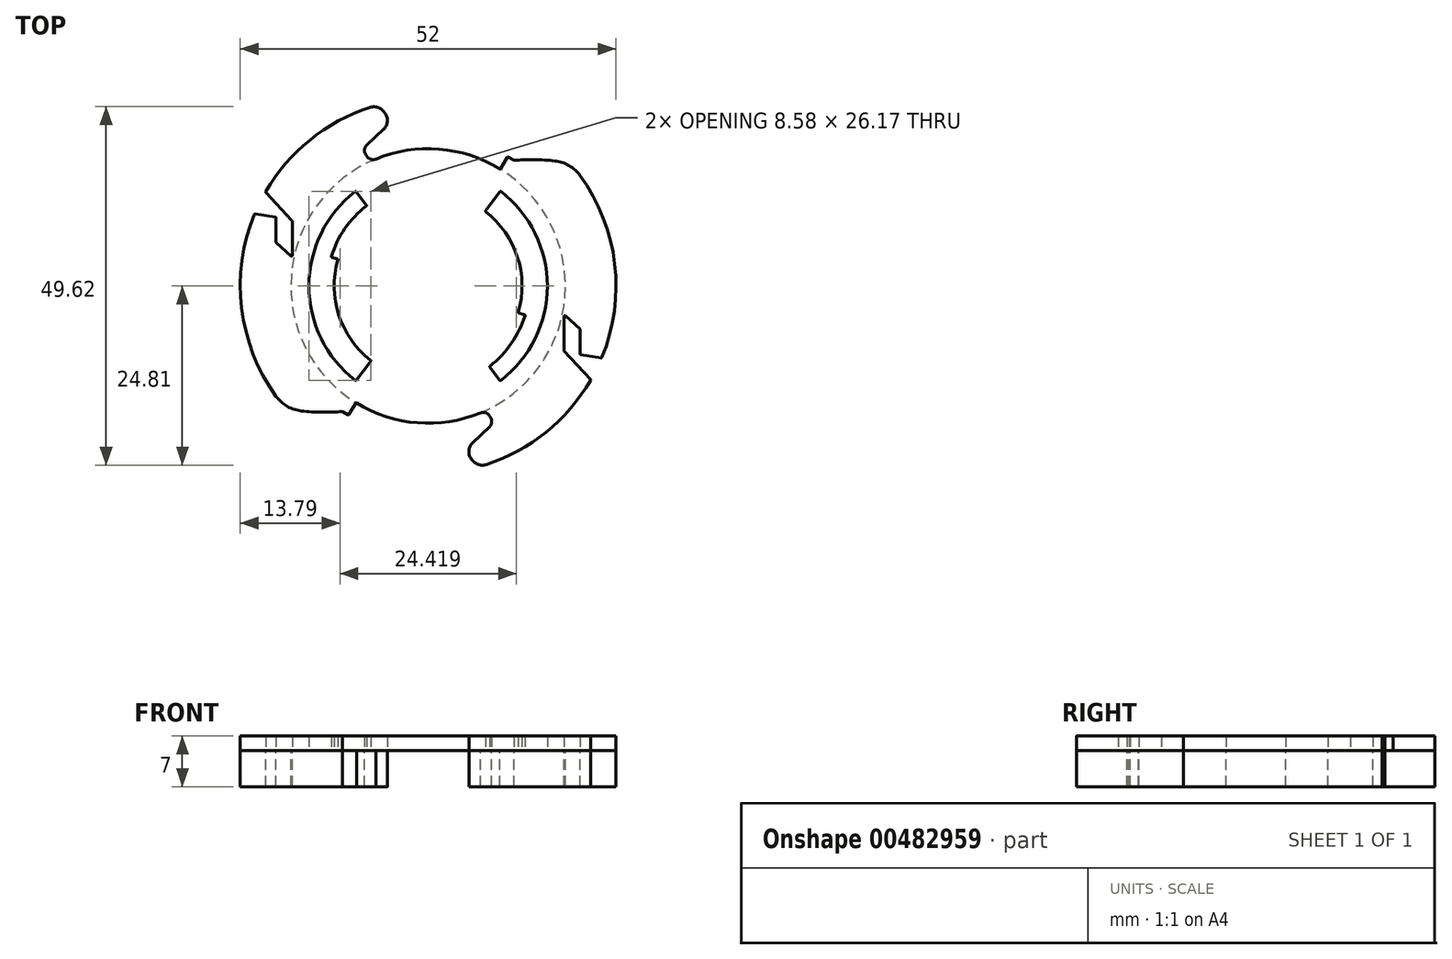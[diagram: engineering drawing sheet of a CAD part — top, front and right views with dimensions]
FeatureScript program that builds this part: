
annotation { "Feature Type Name" : "Feature", "Feature Type Description" : "" }
export const myFeature = defineFeature(function(context is Context, id is Id, definition is map)
    precondition{}
    {
        {
            var Q0;
            Q0=qCreatedBy(makeId("Top.planeOp"),FACE);
            var sketch = newSketch(context, id + "F0", { "sketchPlane" : qUnion([Q0])});
            skArc(sketch, "E0", {"start": v(-9.91, -16.2) * mm, "mid": v(-1.5, -18.94) * mm, "end": v(7.25, -17.56) * mm});
            skArc(sketch, "E1", {"start": v(-10.08, 13.06) * mm, "mid": v(-16.5, 0) * mm, "end": v(-10.08, -13.06) * mm});
            skArc(sketch, "E2", {"start": v(-8.56, 11.08) * mm, "mid": v(-11.52, 7.96) * mm, "end": v(-13.39, 4.1) * mm});
            skArc(sketch, "E3", {"start": v(-12.49, 3.62) * mm, "mid": v(-12.36, -4.03) * mm, "end": v(-7.96, -10.28) * mm});
            skLineSegment(sketch, "E4", {"start": v(-26, 0) * mm, "end": v(26, 0) * mm, "construction": true});
            skLineSegment(sketch, "E5", {"start": v(0, 26) * mm, "end": v(0, -26) * mm, "construction": true});
            skLineSegment(sketch, "E6", {"start": v(9.94, 13.04) * mm, "end": v(7.94, 10.42) * mm});
            skLineSegment(sketch, "E7.MirrorCS", {"start": v(-9.94, 13.04) * mm, "end": v(-8.55, 11.22) * mm});
            skArc(sketch, "E8.trimOffspring", {"start": v(12.49, -3.62) * mm, "mid": v(12.36, 4.03) * mm, "end": v(7.96, 10.28) * mm});
            skArc(sketch, "E9.trimOffspring", {"start": v(8.56, -11.08) * mm, "mid": v(11.52, -7.96) * mm, "end": v(13.39, -4.1) * mm});
            skArc(sketch, "E10.trimOffspring", {"start": v(10.08, -13.06) * mm, "mid": v(16.5, 0) * mm, "end": v(10.08, 13.06) * mm});
            skLineSegment(sketch, "E11", {"start": v(13.32, -3.97) * mm, "end": v(12.55, -3.74) * mm});
            skLineSegment(sketch, "E12.trimOffspring", {"start": v(-7.94, -10.42) * mm, "end": v(-9.94, -13.04) * mm});
            skLineSegment(sketch, "E13.trimOffspring", {"start": v(8.55, -11.22) * mm, "end": v(9.94, -13.04) * mm});
            skLineSegment(sketch, "E14.trimOffspring", {"start": v(-12.55, 3.74) * mm, "end": v(-13.32, 3.97) * mm});
            skPoint(sketch, "E15.visualSharp", {"position": v(-7.94, -19.43) * mm});
            skPoint(sketch, "E16.visualSharp", {"position": v(-3.13, -21.98) * mm});
            skPoint(sketch, "E17.visualSharp", {"position": v(-5, -25.51) * mm});
            skPoint(sketch, "E18.visualSharp", {"position": v(7.94, 19.43) * mm});
            skPoint(sketch, "E19.visualSharp", {"position": v(3.13, 21.98) * mm});
            skPoint(sketch, "E20.visualSharp", {"position": v(5, 25.51) * mm});
            skPoint(sketch, "E21.visualSharp", {"position": v(-8.52, 18.97) * mm});
            skPoint(sketch, "E22.visualSharp", {"position": v(-18.02, 18.75) * mm});
            skPoint(sketch, "E23.visualSharp", {"position": v(18.02, -18.75) * mm});
            skPoint(sketch, "E24.start.orphan", {"position": v(7, 17.66) * mm});
            skPoint(sketch, "E25.start.orphan", {"position": v(7, -17.66) * mm});
            skArc(sketch, "E26", {"start": v(8.04, -24.73) * mm, "mid": v(16.33, -20.23) * mm, "end": v(22.48, -13.06) * mm});
            skLineSegment(sketch, "E27", {"start": v(8.46, -17.93) * mm, "end": v(8.64, -18.2) * mm});
            skLineSegment(sketch, "E28", {"start": v(8.5, -19.48) * mm, "end": v(6.17, -21.7) * mm});
            skLineSegment(sketch, "E29", {"start": v(6.1, -24.1) * mm, "end": v(6.28, -24.28) * mm});
            skLineSegment(sketch, "E30", {"start": v(10.05, 16.24) * mm, "end": v(10.95, 17.8) * mm});
            skLineSegment(sketch, "E31", {"start": v(11.09, 17.84) * mm, "end": v(11.87, 17.39) * mm});
            skArc(sketch, "E32", {"start": v(11.87, 17.39) * mm, "mid": v(14.7, 17.48) * mm, "end": v(17.53, 17.31) * mm});
            skPoint(sketch, "E33.start.orphan", {"position": v(-7, 17.66) * mm});
            skPoint(sketch, "E34.end.orphan", {"position": v(-9.17, 18.2) * mm});
            skPoint(sketch, "E35.start.orphan", {"position": v(-7, -17.66) * mm});
            skArc(sketch, "E36", {"start": v(-8.04, 24.73) * mm, "mid": v(-16.33, 20.23) * mm, "end": v(-22.48, 13.06) * mm});
            skLineSegment(sketch, "E37", {"start": v(-8.46, 17.93) * mm, "end": v(-8.64, 18.2) * mm});
            skLineSegment(sketch, "E38", {"start": v(-8.5, 19.48) * mm, "end": v(-6.17, 21.7) * mm});
            skLineSegment(sketch, "E39", {"start": v(-6.1, 24.1) * mm, "end": v(-6.28, 24.28) * mm});
            skLineSegment(sketch, "E40", {"start": v(-10.05, -16.24) * mm, "end": v(-10.95, -17.8) * mm});
            skLineSegment(sketch, "E41", {"start": v(-11.09, -17.84) * mm, "end": v(-11.87, -17.39) * mm});
            skArc(sketch, "E42", {"start": v(-11.87, -17.39) * mm, "mid": v(-14.7, -17.48) * mm, "end": v(-17.53, -17.31) * mm});
            skArc(sketch, "E43.trimOffspring", {"start": v(9.91, 16.2) * mm, "mid": v(1.5, 18.94) * mm, "end": v(-7.25, 17.56) * mm});
            skCircle(sketch, "E44", {"center": v(0, 0) * mm, "radius": 19 * mm, "construction": true});
            skLineSegment(sketch, "E45", {"start": v(23.92, -9.99) * mm, "end": v(21.13, -9.51) * mm});
            skLineSegment(sketch, "E46", {"start": v(21.04, -9.42) * mm, "end": v(21.04, -6.04) * mm});
            skLineSegment(sketch, "E47", {"start": v(21, -5.97) * mm, "end": v(18.97, -4.15) * mm});
            skLineSegment(sketch, "E48", {"start": v(18.8, -4.22) * mm, "end": v(18.8, -8.96) * mm});
            skLineSegment(sketch, "E49", {"start": v(18.83, -9.03) * mm, "end": v(22.47, -12.95) * mm});
            skArc(sketch, "E50.trimOffspring", {"start": v(24.03, -9.93) * mm, "mid": v(25.82, 3.07) * mm, "end": v(21.04, 15.28) * mm});
            skLineSegment(sketch, "E51", {"start": v(-23.92, 9.99) * mm, "end": v(-21.13, 9.51) * mm});
            skLineSegment(sketch, "E52", {"start": v(-21.04, 9.42) * mm, "end": v(-21.04, 6.04) * mm});
            skLineSegment(sketch, "E53", {"start": v(-21, 5.97) * mm, "end": v(-18.97, 4.15) * mm});
            skLineSegment(sketch, "E54", {"start": v(-18.8, 4.22) * mm, "end": v(-18.8, 8.96) * mm});
            skLineSegment(sketch, "E55", {"start": v(-18.83, 9.03) * mm, "end": v(-22.47, 12.95) * mm});
            skArc(sketch, "E56.trimOffspring", {"start": v(-24.03, 9.93) * mm, "mid": v(-25.82, -3.07) * mm, "end": v(-21.04, -15.28) * mm});
            skPoint(sketch, "E57.visualSharp", {"position": v(8, -17.23) * mm});
            skArc(sketch, "E57.filletArc", {"start": v(8.46, -17.93) * mm, "mid": v(7.92, -17.53) * mm, "end": v(7.25, -17.56) * mm});
            skPoint(sketch, "E58.visualSharp", {"position": v(9.1, -18.9) * mm});
            skArc(sketch, "E58.filletArc", {"start": v(8.5, -19.48) * mm, "mid": v(8.8, -18.87) * mm, "end": v(8.64, -18.2) * mm});
            skPoint(sketch, "E59.visualSharp", {"position": v(4.93, -22.87) * mm});
            skArc(sketch, "E59.filletArc", {"start": v(6.17, -21.7) * mm, "mid": v(5.64, -22.88) * mm, "end": v(6.1, -24.1) * mm});
            skPoint(sketch, "E60.visualSharp", {"position": v(7, -25.04) * mm});
            skArc(sketch, "E60.filletArc", {"start": v(6.28, -24.28) * mm, "mid": v(7.1, -24.76) * mm, "end": v(8.04, -24.73) * mm});
            skPoint(sketch, "E61.visualSharp", {"position": v(-8, 17.23) * mm});
            skArc(sketch, "E61.filletArc", {"start": v(-8.46, 17.93) * mm, "mid": v(-7.92, 17.53) * mm, "end": v(-7.25, 17.56) * mm});
            skPoint(sketch, "E62.visualSharp", {"position": v(-9.1, 18.9) * mm});
            skArc(sketch, "E62.filletArc", {"start": v(-8.5, 19.48) * mm, "mid": v(-8.8, 18.87) * mm, "end": v(-8.64, 18.2) * mm});
            skPoint(sketch, "E63.visualSharp", {"position": v(-4.93, 22.87) * mm});
            skArc(sketch, "E63.filletArc", {"start": v(-6.17, 21.7) * mm, "mid": v(-5.64, 22.88) * mm, "end": v(-6.1, 24.1) * mm});
            skPoint(sketch, "E64.visualSharp", {"position": v(-7, 25.04) * mm});
            skArc(sketch, "E64.filletArc", {"start": v(-6.28, 24.28) * mm, "mid": v(-7.1, 24.76) * mm, "end": v(-8.04, 24.73) * mm});
            skPoint(sketch, "E65.visualSharp", {"position": v(19.67, 17) * mm});
            skArc(sketch, "E65.filletArc", {"start": v(21.04, 15.28) * mm, "mid": v(19.5, 16.67) * mm, "end": v(17.53, 17.31) * mm});
            skPoint(sketch, "E66.visualSharp", {"position": v(-19.67, -17) * mm});
            skArc(sketch, "E66.filletArc", {"start": v(-21.04, -15.28) * mm, "mid": v(-19.5, -16.67) * mm, "end": v(-17.53, -17.31) * mm});
            skPoint(sketch, "E67.visualSharp", {"position": v(-24, 10) * mm});
            skArc(sketch, "E67.filletArc", {"start": v(-23.92, 9.99) * mm, "mid": v(-23.99, 9.98) * mm, "end": v(-24.03, 9.93) * mm});
            skPoint(sketch, "E68.visualSharp", {"position": v(-21.04, 9.5) * mm});
            skArc(sketch, "E68.filletArc", {"start": v(-21.04, 9.42) * mm, "mid": v(-21.07, 9.48) * mm, "end": v(-21.13, 9.51) * mm});
            skPoint(sketch, "E69.visualSharp", {"position": v(-21.04, 6) * mm});
            skArc(sketch, "E69.filletArc", {"start": v(-21.04, 6.04) * mm, "mid": v(-21.03, 6) * mm, "end": v(-21, 5.97) * mm});
            skPoint(sketch, "E70.visualSharp", {"position": v(-18.8, 4) * mm});
            skArc(sketch, "E70.filletArc", {"start": v(-18.97, 4.15) * mm, "mid": v(-18.87, 4.13) * mm, "end": v(-18.8, 4.22) * mm});
            skPoint(sketch, "E71.visualSharp", {"position": v(-18.8, 9) * mm});
            skArc(sketch, "E71.filletArc", {"start": v(-18.8, 8.96) * mm, "mid": v(-18.81, 9) * mm, "end": v(-18.83, 9.03) * mm});
            skPoint(sketch, "E72.visualSharp", {"position": v(-22.52, 13) * mm});
            skArc(sketch, "E72.filletArc", {"start": v(-22.48, 13.06) * mm, "mid": v(-22.5, 13) * mm, "end": v(-22.47, 12.95) * mm});
            skPoint(sketch, "E73.visualSharp", {"position": v(-11, -17.89) * mm});
            skArc(sketch, "E73.filletArc", {"start": v(-11.09, -17.84) * mm, "mid": v(-11.01, -17.85) * mm, "end": v(-10.95, -17.8) * mm});
            skPoint(sketch, "E74.visualSharp", {"position": v(-10, -16.16) * mm});
            skArc(sketch, "E74.filletArc", {"start": v(-9.91, -16.2) * mm, "mid": v(-9.99, -16.2) * mm, "end": v(-10.05, -16.24) * mm});
            skPoint(sketch, "E75.visualSharp", {"position": v(22.52, -13) * mm});
            skArc(sketch, "E75.filletArc", {"start": v(22.48, -13.06) * mm, "mid": v(22.5, -13) * mm, "end": v(22.47, -12.95) * mm});
            skPoint(sketch, "E76.visualSharp", {"position": v(18.8, -9) * mm});
            skArc(sketch, "E76.filletArc", {"start": v(18.8, -8.96) * mm, "mid": v(18.81, -9) * mm, "end": v(18.83, -9.03) * mm});
            skPoint(sketch, "E77.visualSharp", {"position": v(18.8, -4) * mm});
            skArc(sketch, "E77.filletArc", {"start": v(18.97, -4.15) * mm, "mid": v(18.87, -4.13) * mm, "end": v(18.8, -4.22) * mm});
            skPoint(sketch, "E78.visualSharp", {"position": v(21.04, -6) * mm});
            skArc(sketch, "E78.filletArc", {"start": v(21.04, -6.04) * mm, "mid": v(21.03, -6) * mm, "end": v(21, -5.97) * mm});
            skPoint(sketch, "E79.visualSharp", {"position": v(21.04, -9.5) * mm});
            skArc(sketch, "E79.filletArc", {"start": v(21.04, -9.42) * mm, "mid": v(21.07, -9.48) * mm, "end": v(21.13, -9.51) * mm});
            skPoint(sketch, "E80.visualSharp", {"position": v(24, -10) * mm});
            skArc(sketch, "E80.filletArc", {"start": v(23.92, -9.99) * mm, "mid": v(23.99, -9.98) * mm, "end": v(24.03, -9.93) * mm});
            skPoint(sketch, "E81.visualSharp", {"position": v(11, 17.89) * mm});
            skArc(sketch, "E81.filletArc", {"start": v(11.09, 17.84) * mm, "mid": v(11.01, 17.85) * mm, "end": v(10.95, 17.8) * mm});
            skPoint(sketch, "E82.visualSharp", {"position": v(10, 16.16) * mm});
            skArc(sketch, "E82.filletArc", {"start": v(9.91, 16.2) * mm, "mid": v(9.99, 16.2) * mm, "end": v(10.05, 16.24) * mm});
            skPoint(sketch, "E83.visualSharp", {"position": v(10, 13.12) * mm});
            skArc(sketch, "E83.filletArc", {"start": v(10.08, 13.06) * mm, "mid": v(10, 13.08) * mm, "end": v(9.94, 13.04) * mm});
            skPoint(sketch, "E84.visualSharp", {"position": v(7.88, 10.34) * mm});
            skArc(sketch, "E84.filletArc", {"start": v(7.94, 10.42) * mm, "mid": v(7.92, 10.35) * mm, "end": v(7.96, 10.28) * mm});
            skPoint(sketch, "E85.visualSharp", {"position": v(13.42, -4) * mm});
            skArc(sketch, "E85.filletArc", {"start": v(13.39, -4.1) * mm, "mid": v(13.38, -4.02) * mm, "end": v(13.32, -3.97) * mm});
            skPoint(sketch, "E86.visualSharp", {"position": v(12.46, -3.71) * mm});
            skArc(sketch, "E86.filletArc", {"start": v(12.49, -3.62) * mm, "mid": v(12.5, -3.7) * mm, "end": v(12.55, -3.74) * mm});
            skPoint(sketch, "E87.visualSharp", {"position": v(8.48, -11.14) * mm});
            skArc(sketch, "E87.filletArc", {"start": v(8.56, -11.08) * mm, "mid": v(8.53, -11.14) * mm, "end": v(8.55, -11.22) * mm});
            skPoint(sketch, "E88.visualSharp", {"position": v(10, -13.12) * mm});
            skArc(sketch, "E88.filletArc", {"start": v(9.94, -13.04) * mm, "mid": v(10, -13.08) * mm, "end": v(10.08, -13.06) * mm});
            skPoint(sketch, "E89.visualSharp", {"position": v(-10, 13.12) * mm});
            skArc(sketch, "E89.filletArc", {"start": v(-9.94, 13.04) * mm, "mid": v(-10, 13.08) * mm, "end": v(-10.08, 13.06) * mm});
            skPoint(sketch, "E90.visualSharp", {"position": v(-8.48, 11.14) * mm});
            skArc(sketch, "E90.filletArc", {"start": v(-8.56, 11.08) * mm, "mid": v(-8.53, 11.14) * mm, "end": v(-8.55, 11.22) * mm});
            skPoint(sketch, "E91.visualSharp", {"position": v(-13.42, 4) * mm});
            skArc(sketch, "E91.filletArc", {"start": v(-13.39, 4.1) * mm, "mid": v(-13.38, 4.02) * mm, "end": v(-13.32, 3.97) * mm});
            skPoint(sketch, "E92.visualSharp", {"position": v(-12.46, 3.71) * mm});
            skArc(sketch, "E92.filletArc", {"start": v(-12.49, 3.62) * mm, "mid": v(-12.5, 3.7) * mm, "end": v(-12.55, 3.74) * mm});
            skPoint(sketch, "E93.visualSharp", {"position": v(-7.88, -10.34) * mm});
            skArc(sketch, "E93.filletArc", {"start": v(-7.94, -10.42) * mm, "mid": v(-7.92, -10.35) * mm, "end": v(-7.96, -10.28) * mm});
            skPoint(sketch, "E94.visualSharp", {"position": v(-10, -13.12) * mm});
            skArc(sketch, "E94.filletArc", {"start": v(-10.08, -13.06) * mm, "mid": v(-10, -13.08) * mm, "end": v(-9.94, -13.04) * mm});
            skSolve(sketch);
        }
        {
            var Q0;
            Q0 = qSketchRegion(id + "F0", true);
            extrude(context, id + "F1", {"entities" : qUnion([Q0]), "depth" : 2 * mm});
        }
        {
            var Q0;
            Q0=qCreatedBy(makeId("Top.planeOp"),FACE);
            var sketch = newSketch(context, id + "F2", { "sketchPlane" : qUnion([Q0])});
            skArc(sketch, "E95.1", {"start": v(24.03, -9.93) * mm, "mid": v(25.82, 3.07) * mm, "end": v(21.04, 15.28) * mm});
            skLineSegment(sketch, "E96.0", {"start": v(23.92, -9.99) * mm, "end": v(21.13, -9.51) * mm});
            skLineSegment(sketch, "E97.0", {"start": v(21.04, -9.42) * mm, "end": v(21.04, -6.04) * mm});
            skLineSegment(sketch, "E98.0", {"start": v(21, -5.97) * mm, "end": v(18.97, -4.15) * mm});
            skLineSegment(sketch, "E99.0", {"start": v(18.8, -4.22) * mm, "end": v(18.8, -8.96) * mm});
            skLineSegment(sketch, "E100.0", {"start": v(18.83, -9.03) * mm, "end": v(22.47, -12.95) * mm});
            skArc(sketch, "E101.0", {"start": v(8.04, -24.73) * mm, "mid": v(16.33, -20.23) * mm, "end": v(22.48, -13.06) * mm});
            skArc(sketch, "E102.0", {"start": v(6.28, -24.28) * mm, "mid": v(7.1, -24.76) * mm, "end": v(8.04, -24.73) * mm});
            skLineSegment(sketch, "E102.1", {"start": v(6.1, -24.1) * mm, "end": v(6.28, -24.28) * mm});
            skArc(sketch, "E102.2", {"start": v(6.17, -21.7) * mm, "mid": v(5.64, -22.88) * mm, "end": v(6.1, -24.1) * mm});
            skLineSegment(sketch, "E102.3", {"start": v(8.5, -19.48) * mm, "end": v(6.17, -21.7) * mm});
            skArc(sketch, "E103.0", {"start": v(8.46, -17.93) * mm, "mid": v(7.92, -17.53) * mm, "end": v(7.25, -17.56) * mm});
            skLineSegment(sketch, "E103.1", {"start": v(8.46, -17.93) * mm, "end": v(8.64, -18.2) * mm});
            skArc(sketch, "E103.2", {"start": v(8.5, -19.48) * mm, "mid": v(8.8, -18.87) * mm, "end": v(8.64, -18.2) * mm});
            skArc(sketch, "E104.0", {"start": v(22.48, -13.06) * mm, "mid": v(22.5, -13) * mm, "end": v(22.47, -12.95) * mm});
            skArc(sketch, "E105.0", {"start": v(18.8, -8.96) * mm, "mid": v(18.81, -9) * mm, "end": v(18.83, -9.03) * mm});
            skArc(sketch, "E106.0", {"start": v(18.97, -4.15) * mm, "mid": v(18.87, -4.13) * mm, "end": v(18.8, -4.22) * mm});
            skArc(sketch, "E107.0", {"start": v(21.04, -6.04) * mm, "mid": v(21.03, -6) * mm, "end": v(21, -5.97) * mm});
            skArc(sketch, "E108.0", {"start": v(21.04, -9.42) * mm, "mid": v(21.07, -9.48) * mm, "end": v(21.13, -9.51) * mm});
            skArc(sketch, "E109.0", {"start": v(23.92, -9.99) * mm, "mid": v(23.99, -9.98) * mm, "end": v(24.03, -9.93) * mm});
            skLineSegment(sketch, "E110.0", {"start": v(11.09, 17.84) * mm, "end": v(11.87, 17.39) * mm});
            skArc(sketch, "E111.0", {"start": v(11.09, 17.84) * mm, "mid": v(11.01, 17.85) * mm, "end": v(10.95, 17.8) * mm});
            skLineSegment(sketch, "E112.0", {"start": v(10.05, 16.24) * mm, "end": v(10.95, 17.8) * mm});
            skArc(sketch, "E113.0", {"start": v(9.91, 16.2) * mm, "mid": v(9.99, 16.2) * mm, "end": v(10.05, 16.24) * mm});
            skArc(sketch, "E114", {"start": v(7.25, -17.56) * mm, "mid": v(18.94, -1.5) * mm, "end": v(9.91, 16.2) * mm});
            skArc(sketch, "E115.0", {"start": v(21.04, 15.28) * mm, "mid": v(19.5, 16.67) * mm, "end": v(17.53, 17.31) * mm});
            skArc(sketch, "E116.0", {"start": v(11.87, 17.39) * mm, "mid": v(14.7, 17.48) * mm, "end": v(17.53, 17.31) * mm});
            skSolve(sketch);
        }
        {
            var Q0;
            Q0 = qSketchRegion(id + "F2", true);
            extrude(context, id + "F3", {"entities" : qUnion([Q0]), "oppositeDirection" : true, "depth" : 5 * mm});
        }
        {
            var Q0;
            Q0=qCreatedBy(makeId("Top.planeOp"),FACE);
            var sketch = newSketch(context, id + "F4", { "sketchPlane" : qUnion([Q0])});
            skArc(sketch, "E117.0", {"start": v(-8.46, 17.93) * mm, "mid": v(-7.92, 17.53) * mm, "end": v(-7.25, 17.56) * mm});
            skLineSegment(sketch, "E117.1", {"start": v(-8.46, 17.93) * mm, "end": v(-8.64, 18.2) * mm});
            skArc(sketch, "E117.2", {"start": v(-8.5, 19.48) * mm, "mid": v(-8.8, 18.87) * mm, "end": v(-8.64, 18.2) * mm});
            skLineSegment(sketch, "E117.3", {"start": v(-8.5, 19.48) * mm, "end": v(-6.17, 21.7) * mm});
            skArc(sketch, "E118.0", {"start": v(-6.17, 21.7) * mm, "mid": v(-5.64, 22.88) * mm, "end": v(-6.1, 24.1) * mm});
            skArc(sketch, "E119.0", {"start": v(-8.04, 24.73) * mm, "mid": v(-16.33, 20.23) * mm, "end": v(-22.48, 13.06) * mm});
            skArc(sketch, "E119.1", {"start": v(-6.28, 24.28) * mm, "mid": v(-7.1, 24.76) * mm, "end": v(-8.04, 24.73) * mm});
            skLineSegment(sketch, "E119.2", {"start": v(-6.1, 24.1) * mm, "end": v(-6.28, 24.28) * mm});
            skArc(sketch, "E120.0", {"start": v(-22.48, 13.06) * mm, "mid": v(-22.5, 13) * mm, "end": v(-22.47, 12.95) * mm});
            skLineSegment(sketch, "E121.0", {"start": v(-18.83, 9.03) * mm, "end": v(-22.47, 12.95) * mm});
            skArc(sketch, "E122.0", {"start": v(-18.8, 8.96) * mm, "mid": v(-18.81, 9) * mm, "end": v(-18.83, 9.03) * mm});
            skLineSegment(sketch, "E122.1", {"start": v(-18.8, 4.22) * mm, "end": v(-18.8, 8.96) * mm});
            skArc(sketch, "E123.0", {"start": v(-18.97, 4.15) * mm, "mid": v(-18.87, 4.13) * mm, "end": v(-18.8, 4.22) * mm});
            skLineSegment(sketch, "E124.0", {"start": v(-21, 5.97) * mm, "end": v(-18.97, 4.15) * mm});
            skArc(sketch, "E125.0", {"start": v(-21.04, 6.04) * mm, "mid": v(-21.03, 6) * mm, "end": v(-21, 5.97) * mm});
            skLineSegment(sketch, "E125.1", {"start": v(-21.04, 9.42) * mm, "end": v(-21.04, 6.04) * mm});
            skLineSegment(sketch, "E126.0", {"start": v(-23.92, 9.99) * mm, "end": v(-21.13, 9.51) * mm});
            skArc(sketch, "E126.1", {"start": v(-21.04, 9.42) * mm, "mid": v(-21.07, 9.48) * mm, "end": v(-21.13, 9.51) * mm});
            skArc(sketch, "E127.0", {"start": v(-24.03, 9.93) * mm, "mid": v(-25.82, -3.07) * mm, "end": v(-21.04, -15.28) * mm});
            skArc(sketch, "E127.1", {"start": v(-23.92, 9.99) * mm, "mid": v(-23.99, 9.98) * mm, "end": v(-24.03, 9.93) * mm});
            skArc(sketch, "E128.0", {"start": v(-11.87, -17.39) * mm, "mid": v(-14.7, -17.48) * mm, "end": v(-17.53, -17.31) * mm});
            skArc(sketch, "E128.1", {"start": v(-21.04, -15.28) * mm, "mid": v(-19.5, -16.67) * mm, "end": v(-17.53, -17.31) * mm});
            skLineSegment(sketch, "E129.0", {"start": v(-11.09, -17.84) * mm, "end": v(-11.87, -17.39) * mm});
            skArc(sketch, "E129.1", {"start": v(-11.09, -17.84) * mm, "mid": v(-11.01, -17.85) * mm, "end": v(-10.95, -17.8) * mm});
            skLineSegment(sketch, "E130.0", {"start": v(-10.05, -16.24) * mm, "end": v(-10.95, -17.8) * mm});
            skArc(sketch, "E131.0", {"start": v(-9.91, -16.2) * mm, "mid": v(-9.99, -16.2) * mm, "end": v(-10.05, -16.24) * mm});
            skArc(sketch, "E132", {"start": v(-7.25, 17.56) * mm, "mid": v(-18.94, 1.5) * mm, "end": v(-9.91, -16.2) * mm});
            skSolve(sketch);
        }
        {
            var Q0;
            Q0 = qSketchRegion(id + "F4", true);
            extrude(context, id + "F5", {"entities" : qUnion([Q0]), "oppositeDirection" : true, "depth" : 5 * mm});
        }
    });
